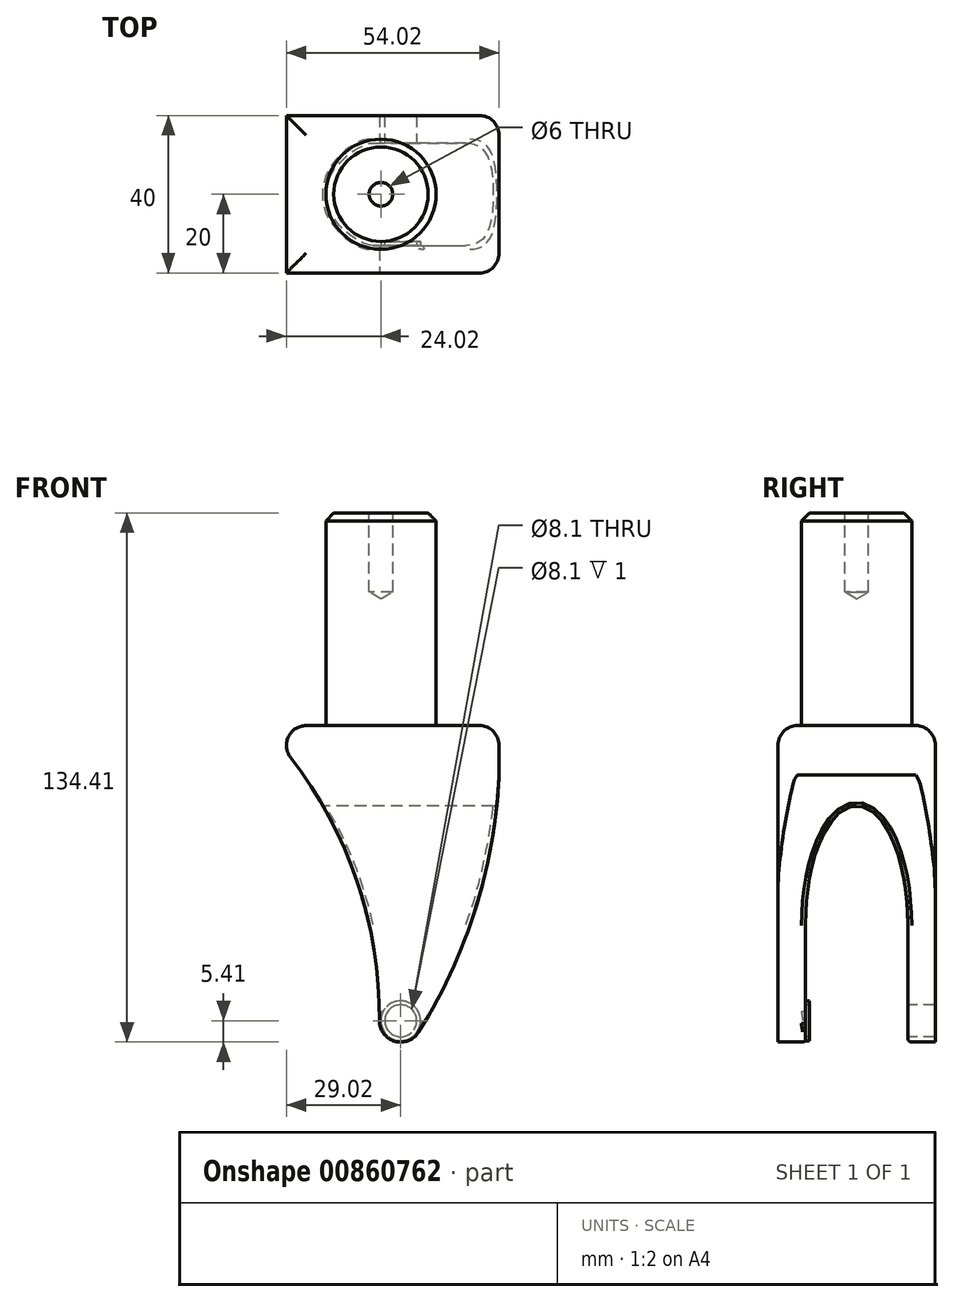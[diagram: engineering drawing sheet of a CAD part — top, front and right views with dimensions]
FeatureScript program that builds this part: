
annotation { "Feature Type Name" : "Feature", "Feature Type Description" : "" }
export const myFeature = defineFeature(function(context is Context, id is Id, definition is map)
    precondition{}
    {
        {
            var Q0;
            Q0=qCreatedBy(makeId("Top.planeOp"),FACE);
            var sketch = newSketch(context, id + "F0", { "sketchPlane" : qUnion([Q0])});
            skCircle(sketch, "E0", {"center": v(0, 0) * mm, "radius": 14 * mm});
            skSolve(sketch);
        }
        {
            var Q0;
            Q0=qSketchRegion(id+"F0",true);
            extrude(context, id + "F1", {"entities" : qUnion([Q0]), "depth" : 144 * mm, "offsetDistance" : 25 * mm});
        }
        {
            var Q0;
            Q0=qCreatedBy(makeId("Top.planeOp"),FACE);
            var sketch = newSketch(context, id + "F2", { "sketchPlane" : qUnion([Q0])});
            skLineSegment(sketch, "E1.bottom", {"start": v(30, -20) * mm, "end": v(-30, -20) * mm});
            skLineSegment(sketch, "E1.top", {"start": v(30, 20) * mm, "end": v(-30, 20) * mm});
            skLineSegment(sketch, "E1.left", {"start": v(30, -20) * mm, "end": v(30, 20) * mm});
            skLineSegment(sketch, "E1.right", {"start": v(-30, -20) * mm, "end": v(-30, 20) * mm});
            skPoint(sketch, "E1.middle", {"position": v(0, 0) * mm});
            skSolve(sketch);
        }
        {
            var Q0;
            Q0=qSketchRegion(id+"F2",true);
            extrude(context, id + "F3", {"entities" : qUnion([Q0]), "operationType" : NewBodyOperationType.ADD, "depth" : 90 * mm, "offsetDistance" : 25 * mm});
        }
        {
            var Q0;
            Q0=makeQuery(id+"F3.opExtrude","SWEPT_EDGE",EDGE,{"disambiguationData":[OSD([sQuery(id+"F2.wireOp",EDGE,"E1.bottom"),sQuery(id+"F2.wireOp",EDGE,"E1.left")])]});
            var Q1;
            Q1=makeQuery(id+"F3.opExtrude","SWEPT_EDGE",EDGE,{"disambiguationData":[OSD([sQuery(id+"F2.wireOp",EDGE,"E1.top"),sQuery(id+"F2.wireOp",EDGE,"E1.left")])]});
            var Q2;
            Q2=makeQuery(id+"F3.opExtrude","SWEPT_EDGE",EDGE,{"disambiguationData":[OSD([sQuery(id+"F2.wireOp",EDGE,"E1.bottom"),sQuery(id+"F2.wireOp",EDGE,"E1.right")])]});
            var Q3;
            Q3=makeQuery(id+"F3.opExtrude","SWEPT_EDGE",EDGE,{"disambiguationData":[OSD([sQuery(id+"F2.wireOp",EDGE,"E1.top"),sQuery(id+"F2.wireOp",EDGE,"E1.right")])]});
            fillet(context, id + "F4", {"entities" : qUnion([Q0, Q1, Q2, Q3]), "radius" : 5 * mm, "tangentPropagation" : true, "allowEdgeOverflow" : false});
        }
        {
            var Q0;
            Q0=qCreatedBy(makeId("Front.planeOp"),FACE);
            var sketch = newSketch(context, id + "F5", { "sketchPlane" : qUnion([Q0])});
            skArc(sketch, "E2", {"start": v(-0.41, 15.04) * mm, "mid": v(-9.5, 59.24) * mm, "end": v(-35.86, 95.87) * mm});
            skArc(sketch, "E3", {"start": v(9.59, 12.13) * mm, "mid": v(25.73, 49.5) * mm, "end": v(30, 90) * mm});
            skArc(sketch, "E4", {"start": v(-57.39, 108.68) * mm, "mid": v(-46.85, 101.9) * mm, "end": v(-35.86, 95.87) * mm});
            skArc(sketch, "E5", {"start": v(-0.41, 15.04) * mm, "mid": v(3.49, 9.8) * mm, "end": v(9.59, 12.13) * mm});
            skPoint(sketch, "E6", {"position": v(-29.93, 90.06) * mm});
            skLineSegment(sketch, "E7", {"start": v(-35.86, 95.87) * mm, "end": v(-35.86, -7.4) * mm});
            skLineSegment(sketch, "E8", {"start": v(-35.86, -7.4) * mm, "end": v(57.44, -7.4) * mm});
            skLineSegment(sketch, "E9", {"start": v(57.44, -7.4) * mm, "end": v(53.15, 90.2) * mm});
            skLineSegment(sketch, "E10", {"start": v(53.15, 90.2) * mm, "end": v(30, 90) * mm});
            skSolve(sketch);
        }
        {
            var Q0;
            Q0=qSketchRegion(id+"F5",true);
            extrude(context, id + "F6", {"entities" : qUnion([Q0]), "operationType" : NewBodyOperationType.REMOVE, "endBound" : BoundingType.SYMMETRIC, "oppositeDirection" : true, "depth" : 80 * mm, "offsetDistance" : 25 * mm});
        }
        {
            var Q0;
            Q0=qCreatedBy(makeId("Right.planeOp"),FACE);
            var sketch = newSketch(context, id + "F7", { "sketchPlane" : qUnion([Q0])});
            skEllipticalArc(sketch, "E11", {});
            skLineSegment(sketch, "E12", {"start": v(-13, 39.54) * mm, "end": v(-13, -0.46) * mm});
            skLineSegment(sketch, "E13", {"start": v(13, -0.46) * mm, "end": v(13, 39.54) * mm});
            skLineSegment(sketch, "E14", {"start": v(-13, -0.46) * mm, "end": v(13, -0.46) * mm});
            skLineSegment(sketch, "E15", {"start": v(-0.05, -0.46) * mm, "end": v(0.07, -0.46) * mm, "construction": true});
            skPoint(sketch, "E16", {"position": v(0, -0.46) * mm});
            skLineSegment(sketch, "E17", {"start": v(0, 69.59) * mm, "end": v(0.07, -0.46) * mm, "construction": true});
            skLineSegment(sketch, "E18", {"start": v(0, 90) * mm, "end": v(0.07, -0.46) * mm, "construction": true});
            const initialGuessF7  = {"E11": [0, 0.03954439638786203, 0, -1, 0.030045165160303693, 0.013, 1.5707963267948966, 4.71238898038469]};
            skSetInitialGuess(sketch, initialGuessF7);
            skSolve(sketch);
        }
        {
            var Q0;
            Q0=qSketchRegion(id+"F7",true);
            extrude(context, id + "F8", {"entities" : qUnion([Q0]), "operationType" : NewBodyOperationType.REMOVE, "endBound" : BoundingType.SYMMETRIC, "oppositeDirection" : true, "depth" : 70 * mm, "offsetDistance" : 25 * mm});
        }
        {
            var Q0;
            Q0=qCreatedBy(makeId("Front.planeOp"),FACE);
            var sketch = newSketch(context, id + "F9", { "sketchPlane" : qUnion([Q0])});
            skPoint(sketch, "E19", {"position": v(5, 15) * mm});
            skSolve(sketch);
        }
        {
            var Q0;
            Q0=sQuery(id+"F9.wireOp",VERTEX,"E19");
            var Q1;
            Q1=makeQuery(id+"F1.opExtrude","SWEPT_BODY",BODY,{"disambiguationData":[OSD([sQuery(id+"F0.wireOp",EDGE,"E0")])]});
            hole(context, id + "F10", {"style" : HoleStyle.SIMPLE, "endStyle" : HoleEndStyle.BLIND, "holeDiameter" : 8.1 * mm, "majorDiameter" : 5 * mm, "holeDepth" : 30 * mm, "isTappedThrough" : true, "tappedDepth" : 12 * mm, "tapClearance" : 3, "locations" : qUnion([Q0]), "scope" : qUnion([Q1])});
        }
        {
            var Q0;
            Q0=makeQuery(id+"F8.boolean.opBoolean","COPY",FACE,{"derivedFrom":makeQuery(id+"F8.opExtrude","SWEPT_FACE",FACE,{"disambiguationData":[OSD([sQuery(id+"F7.wireOp",EDGE,"E12")])]})});
            var sketch = newSketch(context, id + "F11", { "sketchPlane" : qUnion([Q0])});
            skCircle(sketch, "E20.0", {"center": v(-5, 15) * mm, "radius": 4.05 * mm});
            skCircle(sketch, "E21.0", {"center": v(-5, 15) * mm, "radius": 5.05 * mm});
            skSolve(sketch);
        }
        {
            var Q0;
            Q0=makeQuery(id+"F11.imprint","IMPRINT",FACE,{"disambiguationData":[TD([[makeQuery(id+"F11.imprint","IMPRINT",EDGE,{"derivedFrom":sQuery(id+"F11.wireOp",EDGE,"E20.0")}),-1.0]])]});
            var Q1;
            Q1=qConstructionFilter(qBodyType(qCreatedBy(id+"F11",EDGE),BodyType.WIRE),ConstructionObject.NO);
            extrude(context, id + "F12", {"entities" : qUnion([Q0]), "operationType" : NewBodyOperationType.ADD, "surfaceOperationType" : NewSurfaceOperationType.ADD, "surfaceEntities" : qUnion([Q1]), "depth" : 1 * mm, "offsetDistance" : 25 * mm});
        }
        {
            var Q0;
            Q0=makeQuery(id+"F1.opExtrude","CAP_FACE",FACE,{"disambiguationData":[OSD([sQuery(id+"F0.wireOp",EDGE,"E0")])],"isStart":false});
            var sketch = newSketch(context, id + "F13", { "sketchPlane" : qUnion([Q0])});
            skPoint(sketch, "E22", {"position": v(0, 0) * mm});
            skSolve(sketch);
        }
        {
            var Q0;
            Q0=sQuery(id+"F13.wireOp",VERTEX,"E22");
            var Q1;
            Q1=makeQuery(id+"F1.opExtrude","SWEPT_BODY",BODY,{"disambiguationData":[OSD([sQuery(id+"F0.wireOp",EDGE,"E0")])]});
            hole(context, id + "F14", {"style" : HoleStyle.SIMPLE, "endStyle" : HoleEndStyle.BLIND, "holeDiameter" : 6 * mm, "majorDiameter" : 5 * mm, "holeDepth" : 20 * mm, "isTappedThrough" : true, "tappedDepth" : 12 * mm, "tapClearance" : 3, "locations" : qUnion([Q0]), "scope" : qUnion([Q1])});
        }
        {
            var Q0;
            Q0=makeQuery(id+"F1.opExtrude","CAP_EDGE",EDGE,{"disambiguationData":[OSD([sQuery(id+"F0.wireOp",EDGE,"E0")])],"isStart":false});
            chamfer(context, id + "F15", {"entities" : qUnion([Q0]), "width" : 2 * mm, "tangentPropagation" : true});
        }
        {
            var Q0;
            Q0=makeQuery(id+"F8.boolean.opBoolean","INTERSECT",EDGE,{"derivedFrom":[makeQuery(id+"F6.boolean.opBoolean","COPY",FACE,{"derivedFrom":makeQuery(id+"F6.opExtrude","SWEPT_FACE",FACE,{"disambiguationData":[OSD([sQuery(id+"F5.wireOp",EDGE,"E3")])]})}),makeQuery(id+"F8.opExtrude","SWEPT_FACE",FACE,{"disambiguationData":[OSD([sQuery(id+"F7.wireOp",EDGE,"E11")])]})]});
            var Q1;
            Q1=makeQuery(id+"F8.boolean.opBoolean","INTERSECT",EDGE,{"derivedFrom":[makeQuery(id+"F6.boolean.opBoolean","COPY",FACE,{"derivedFrom":makeQuery(id+"F6.opExtrude","SWEPT_FACE",FACE,{"disambiguationData":[OSD([sQuery(id+"F5.wireOp",EDGE,"E2")])]})}),makeQuery(id+"F8.opExtrude","SWEPT_FACE",FACE,{"disambiguationData":[OSD([sQuery(id+"F7.wireOp",EDGE,"E11")])]})]});
            fillet(context, id + "F16", {"entities" : qUnion([Q0, Q1]), "radius" : 1 * mm, "tangentPropagation" : true, "allowEdgeOverflow" : false});
        }
        {
            var Q0;
            Q0=makeQuery(id+"F3.opExtrude","CAP_EDGE",EDGE,{"disambiguationData":[OSD([sQuery(id+"F2.wireOp",EDGE,"E1.bottom")])],"isStart":false});
            var Q1;
            Q1=makeQuery(id+"F3.opExtrude","CAP_EDGE",EDGE,{"disambiguationData":[OSD([sQuery(id+"F2.wireOp",EDGE,"E1.top")])],"isStart":false});
            var Q2;
            Q2=makeQuery(id+"F6.boolean.opBoolean","INTERSECT",EDGE,{"derivedFrom":[makeQuery(id+"F3.opExtrude","CAP_FACE",FACE,{"disambiguationData":[OSD([sQuery(id+"F2.wireOp",EDGE,"E1.bottom"),sQuery(id+"F2.wireOp",EDGE,"E1.top"),sQuery(id+"F2.wireOp",EDGE,"E1.left"),sQuery(id+"F2.wireOp",EDGE,"E1.right")])],"isStart":false}),makeQuery(id+"F6.opExtrude","SWEPT_FACE",FACE,{"disambiguationData":[OSD([sQuery(id+"F5.wireOp",EDGE,"E2")])]})]});
            fillet(context, id + "F17", {"entities" : qUnion([Q0, Q1, Q2]), "radius" : 5 * mm, "allowEdgeOverflow" : false});
        }
        {
            var Q0;
            Q0=makeQuery(id+"F3.opExtrude","CAP_EDGE",EDGE,{"disambiguationData":[OSD([sQuery(id+"F2.wireOp",EDGE,"E1.left")])],"isStart":false});
            fillet(context, id + "F18", {"entities" : qUnion([Q0]), "radius" : 5 * mm, "tangentPropagation" : true, "allowEdgeOverflow" : false});
        }
    });
